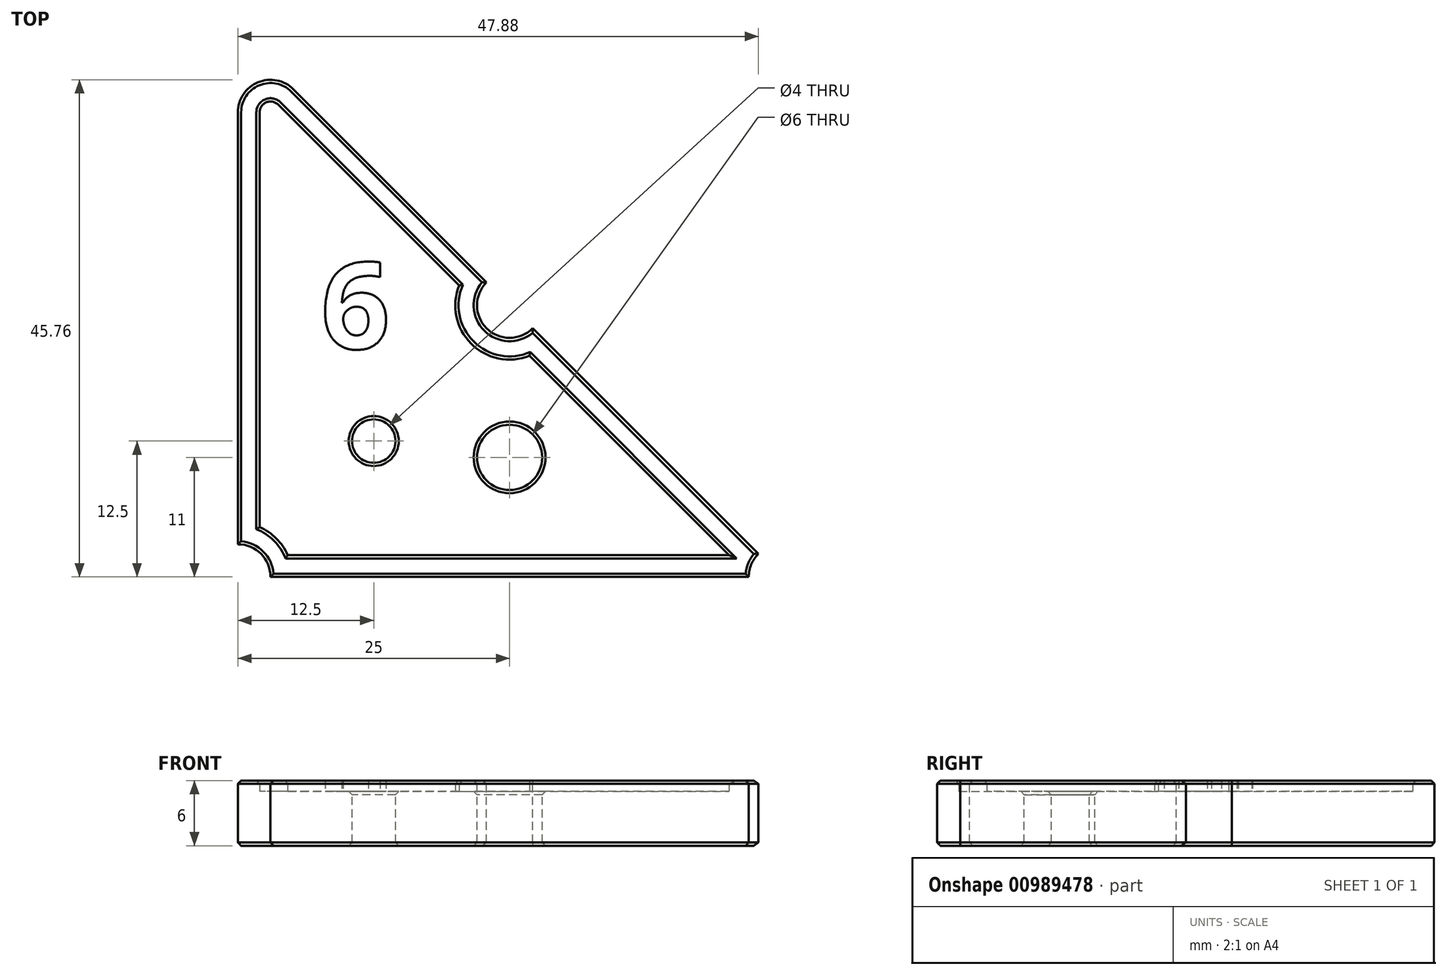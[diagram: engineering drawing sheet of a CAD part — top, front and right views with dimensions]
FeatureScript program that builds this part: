
annotation { "Feature Type Name" : "Feature", "Feature Type Description" : "" }
export const myFeature = defineFeature(function(context is Context, id is Id, definition is map)
    precondition{}
    {
        {
            var Q0;
            Q0=qCreatedBy(makeId("Top.planeOp"),FACE);
            var sketch = newSketch(context, id + "F0", { "sketchPlane" : qUnion([Q0])});
            skLineSegment(sketch, "E0", {"start": v(-25, 25) * mm, "end": v(-25, -25) * mm});
            skLineSegment(sketch, "E1", {"start": v(-25, -25) * mm, "end": v(25, -25) * mm});
            skLineSegment(sketch, "E2", {"start": v(25, -25) * mm, "end": v(-25, 25) * mm});
            skPoint(sketch, "E3", {"position": v(0, 0) * mm});
            skCircle(sketch, "E4", {"center": v(-25, -25) * mm, "radius": 3 * mm});
            skCircle(sketch, "E5", {"center": v(25, -25) * mm, "radius": 3 * mm});
            skCircle(sketch, "E6", {"center": v(0, 0) * mm, "radius": 3 * mm});
            skArc(sketch, "E7", {"start": v(-19.88, 19.88) * mm, "mid": v(-23.15, 20.53) * mm, "end": v(-25, 17.76) * mm});
            skCircle(sketch, "E8", {"center": v(-12.5, -12.5) * mm, "radius": 2 * mm});
            skLineSegment(sketch, "E9", {"start": v(0, 0) * mm, "end": v(-25, -25) * mm, "construction": true});
            skCircle(sketch, "E10", {"center": v(0, -14) * mm, "radius": 3 * mm});
            skLineSegment(sketch, "E11", {"start": v(0, -3) * mm, "end": v(0, -25) * mm, "construction": true});
            skPoint(sketch, "E11.startSnap0", {"position": v(0, -25) * mm});
            skLineSegment(sketch, "E12", {"start": v(-3, 3) * mm, "end": v(-3, -7.3) * mm, "construction": true});
            skLineSegment(sketch, "E13", {"start": v(-3, 0) * mm, "end": v(-25, 0) * mm, "construction": true});
            skText(sketch, "E14", { "text": "6", "fontName": "OpenSans-Bold.ttf"});
            skPoint(sketch, "E15", {"position": v(-14, 0) * mm});
            const initialGuessF0  = {"E14": [-0.01736, -0.004, 1, 0, 0.008]};
            skSetInitialGuess(sketch, initialGuessF0);
            skSolve(sketch);
        }
        {
            var Q0;
            {var subQ5=sQuery(id+"F0.wireOp",EDGE,"E7");Q0=makeQuery(id+"F0.imprint","IMPRINT",FACE,{"disambiguationData":[TD([[makeQuery(id+"F0.imprint","IMPRINT",EDGE,{"derivedFrom":subQ5}),1.0]])]});}
            var Q1;
            Q1=makeQuery(id+"F0.imprint","IMPRINT",FACE,{"disambiguationData":[TD([[makeQuery(id+"F0.imprint","IMPRINT",EDGE,{"derivedFrom":sQuery(id+"F0.wireOp",EDGE,"E14.sketch_text.stroke-0")}),-1.0]])]});
            var Q2;
            Q2=makeQuery(id+"F0.imprint","IMPRINT",FACE,{"disambiguationData":[TD([[makeQuery(id+"F0.imprint","IMPRINT",EDGE,{"derivedFrom":sQuery(id+"F0.wireOp",EDGE,"E14.sketch_text.stroke-17")}),1.0]])]});
            extrude(context, id + "F1", {"entities" : qUnion([Q0, Q1, Q2]), "oppositeDirection" : true, "depth" : 5 * mm, "offsetDistance" : 25 * mm});
        }
        {
            var Q0;
            Q0=makeQuery(id+"F1.opExtrude","CAP_FACE",FACE,{"disambiguationData":[OSD([sQuery(id+"F0.wireOp",EDGE,"E0"),sQuery(id+"F0.wireOp",EDGE,"E1"),sQuery(id+"F0.wireOp",EDGE,"E2"),sQuery(id+"F0.wireOp",EDGE,"E4"),sQuery(id+"F0.wireOp",EDGE,"E5"),sQuery(id+"F0.wireOp",EDGE,"E6"),sQuery(id+"F0.wireOp",EDGE,"E7"),sQuery(id+"F0.wireOp",EDGE,"E8"),sQuery(id+"F0.wireOp",EDGE,"E10")])],"isStart":true});
            var sketch = newSketch(context, id + "F2", { "sketchPlane" : qUnion([Q0])});
            skLineSegment(sketch, "E16.0", {"start": v(20.17, -23) * mm, "end": v(1.83, -4.65) * mm});
            skLineSegment(sketch, "E16.1", {"start": v(-20.42, -23) * mm, "end": v(20.17, -23) * mm});
            skLineSegment(sketch, "E16.2", {"start": v(-4.65, 1.83) * mm, "end": v(-21.3, 18.46) * mm});
            skArc(sketch, "E16.3", {"start": v(-21.3, 18.46) * mm, "mid": v(-22.38, 18.68) * mm, "end": v(-23, 17.76) * mm});
            skLineSegment(sketch, "E16.4", {"start": v(-23, 17.76) * mm, "end": v(-23, -20.42) * mm});
            skArc(sketch, "E16.5", {"start": v(1.83, -4.65) * mm, "mid": v(-3.54, -3.54) * mm, "end": v(-4.65, 1.83) * mm});
            skArc(sketch, "E16.6", {"start": v(-23, -20.42) * mm, "mid": v(-21.46, -21.46) * mm, "end": v(-20.42, -23) * mm});
            skSolve(sketch);
        }
        {
            var Q0;
            Q0=makeQuery(id+"F0.imprint","IMPRINT",FACE,{"disambiguationData":[TD([[makeQuery(id+"F0.imprint","IMPRINT",EDGE,{"derivedFrom":sQuery(id+"F0.wireOp",EDGE,"E14.sketch_text.stroke-0")}),-1.0]])]});
            var Q1;
            Q1=makeQuery(id+"F2.imprint","IMPRINT",FACE,{"disambiguationData":[TD([[makeQuery(id+"F2.imprint","IMPRINT",EDGE,{"derivedFrom":sQuery(id+"F2.wireOp",EDGE,"E16.0")}),-1.0]])]});
            extrude(context, id + "F3", {"entities" : qUnion([Q0, Q1]), "operationType" : NewBodyOperationType.ADD, "depth" : 1 * mm, "offsetDistance" : 25 * mm});
        }
        {
            var Q0;
            Q0=makeQuery(id+"F3.opExtrude","CAP_FACE",FACE,{"disambiguationData":[OSD([sQuery(id+"F0.wireOp",EDGE,"E0"),sQuery(id+"F0.wireOp",EDGE,"E1"),sQuery(id+"F0.wireOp",EDGE,"E2"),sQuery(id+"F0.wireOp",EDGE,"E4"),sQuery(id+"F0.wireOp",EDGE,"E5"),sQuery(id+"F0.wireOp",EDGE,"E6"),sQuery(id+"F0.wireOp",EDGE,"E7"),sQuery(id+"F2.wireOp",EDGE,"E16.0"),sQuery(id+"F2.wireOp",EDGE,"E16.1"),sQuery(id+"F2.wireOp",EDGE,"E16.2"),sQuery(id+"F2.wireOp",EDGE,"E16.3"),sQuery(id+"F2.wireOp",EDGE,"E16.4"),sQuery(id+"F2.wireOp",EDGE,"E16.5"),sQuery(id+"F2.wireOp",EDGE,"E16.6")])],"isStart":false});
            var Q1;
            Q1=makeQuery(id+"F1.opExtrude","CAP_EDGE",EDGE,{"disambiguationData":[OSD([sQuery(id+"F0.wireOp",EDGE,"E8")])],"isStart":true});
            var Q2;
            Q2=makeQuery(id+"F1.opExtrude","CAP_EDGE",EDGE,{"disambiguationData":[OSD([sQuery(id+"F0.wireOp",EDGE,"E10")])],"isStart":true});
            var Q3;
            Q3=makeQuery(id+"F1.opExtrude","CAP_FACE",FACE,{"disambiguationData":[OSD([sQuery(id+"F0.wireOp",EDGE,"E0"),sQuery(id+"F0.wireOp",EDGE,"E1"),sQuery(id+"F0.wireOp",EDGE,"E2"),sQuery(id+"F0.wireOp",EDGE,"E4"),sQuery(id+"F0.wireOp",EDGE,"E5"),sQuery(id+"F0.wireOp",EDGE,"E6"),sQuery(id+"F0.wireOp",EDGE,"E7"),sQuery(id+"F0.wireOp",EDGE,"E8"),sQuery(id+"F0.wireOp",EDGE,"E10")])],"isStart":false});
            chamfer(context, id + "F4", {"entities" : qUnion([Q0, Q1, Q2, Q3]), "width" : 0.3 * mm, "tangentPropagation" : true});
        }
    });
